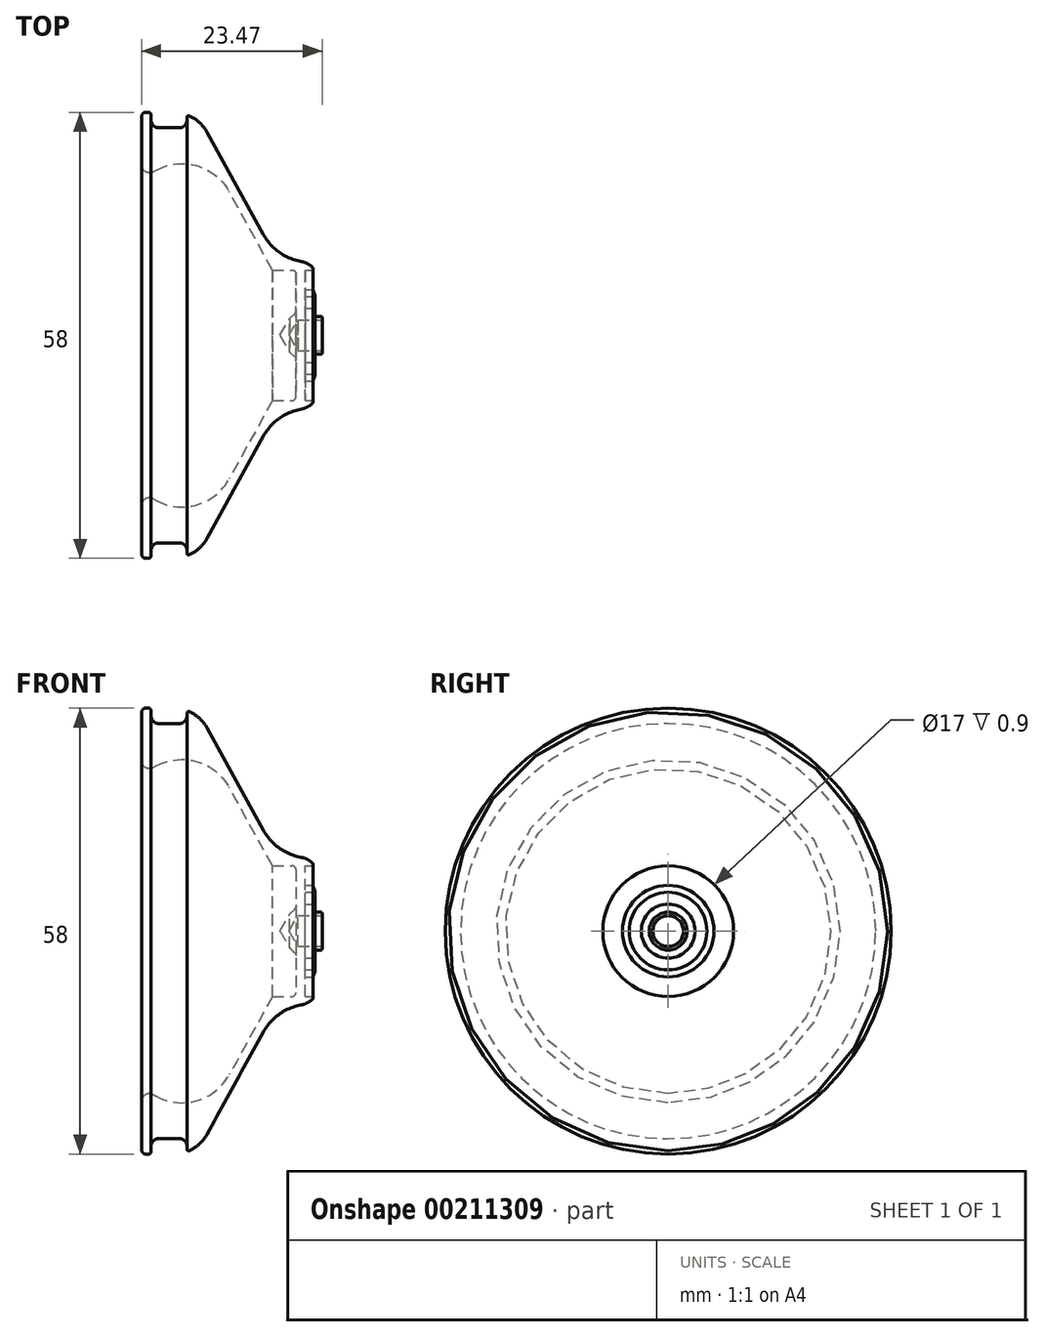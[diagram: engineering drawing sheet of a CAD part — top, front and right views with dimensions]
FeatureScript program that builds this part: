
annotation { "Feature Type Name" : "Feature", "Feature Type Description" : "" }
export const myFeature = defineFeature(function(context is Context, id is Id, definition is map)
    precondition{}
    {
        {
            var Q0;
            Q0=qCreatedBy(makeId("Front.planeOp"),FACE);
            var sketch = newSketch(context, id + "F0", { "sketchPlane" : qUnion([Q0])});
            skLineSegment(sketch, "E0", {"start": v(-1.03, 2) * mm, "end": v(-4.2, 2) * mm});
            skLineSegment(sketch, "E1", {"start": v(-4.2, 2) * mm, "end": v(-5.35, 0) * mm});
            skLineSegment(sketch, "E2", {"start": v(-5.35, 0) * mm, "end": v(-6.5, 0) * mm});
            skLineSegment(sketch, "E3", {"start": v(-6.5, 0) * mm, "end": v(-5.24, 2.2) * mm});
            skLineSegment(sketch, "E4", {"start": v(-4.45, 8.5) * mm, "end": v(-7.5, 8.5) * mm});
            skLineSegment(sketch, "E5", {"start": v(-7.5, 8.5) * mm, "end": v(-13.13, 18.7) * mm});
            skLineSegment(sketch, "E6", {"start": v(-24.5, 22.13) * mm, "end": v(-24.5, 29) * mm});
            skLineSegment(sketch, "E7", {"start": v(-24.5, 29) * mm, "end": v(-23.6, 29) * mm});
            skLineSegment(sketch, "E8", {"start": v(-1.03, 2.47) * mm, "end": v(-2.03, 2.47) * mm});
            skLineSegment(sketch, "E9", {"start": v(-2.03, 2.47) * mm, "end": v(-2.03, 3.5) * mm});
            skLineSegment(sketch, "E10", {"start": v(-2.03, 3.5) * mm, "end": v(-3.25, 3.5) * mm});
            skLineSegment(sketch, "E11", {"start": v(-3.25, 3.5) * mm, "end": v(-3.25, 5.05) * mm});
            skLineSegment(sketch, "E12", {"start": v(-3.25, 5.05) * mm, "end": v(-1.9, 5.05) * mm});
            skLineSegment(sketch, "E13", {"start": v(-2.25, 5.95) * mm, "end": v(-3.25, 5.95) * mm});
            skLineSegment(sketch, "E14", {"start": v(-3.25, 5.95) * mm, "end": v(-3.25, 8.5) * mm});
            skLineSegment(sketch, "E15", {"start": v(-3.25, 8.5) * mm, "end": v(-2.25, 8.5) * mm});
            skLineSegment(sketch, "E16", {"start": v(-2.25, 8.5) * mm, "end": v(-2.25, 9.5) * mm});
            skLineSegment(sketch, "E17", {"start": v(-1.03, 2.47) * mm, "end": v(-1.03, 2) * mm});
            skLineSegment(sketch, "E18", {"start": v(-2.25, 9.5) * mm, "end": v(-2.25, 9.5) * mm});
            skLineSegment(sketch, "E19", {"start": v(-4.45, 8.5) * mm, "end": v(-4.45, 3) * mm});
            skLineSegment(sketch, "E20", {"start": v(-4.45, 3) * mm, "end": v(-5.24, 2.2) * mm});
            skLineSegment(sketch, "E21", {"start": v(-2.25, 9.5) * mm, "end": v(-2.55, 9.5) * mm});
            skLineSegment(sketch, "E22", {"start": v(-16, 26.41) * mm, "end": v(-8.69, 13.12) * mm});
            skPoint(sketch, "E23.visualSharp", {"position": v(-6.7, 9.5) * mm});
            skArc(sketch, "E23.filletArc", {"start": v(-8.69, 13.12) * mm, "mid": v(-6.11, 10.47) * mm, "end": v(-2.55, 9.5) * mm});
            skPoint(sketch, "E24.visualSharp", {"position": v(-17.43, 29) * mm});
            skArc(sketch, "E24.filletArc", {"start": v(-16, 26.41) * mm, "mid": v(-16.99, 27.67) * mm, "end": v(-18.32, 28.55) * mm});
            skLineSegment(sketch, "E25", {"start": v(-23.03, 21.25) * mm, "end": v(-22.57, 21.5) * mm});
            skPoint(sketch, "E26.visualSharp", {"position": v(-16.47, 24.77) * mm});
            skArc(sketch, "E26.filletArc", {"start": v(-13.13, 18.7) * mm, "mid": v(-17.27, 22.04) * mm, "end": v(-22.57, 21.5) * mm});
            skPoint(sketch, "E27.visualSharp", {"position": v(-24.5, 20.46) * mm});
            skLineSegment(sketch, "E28", {"start": v(-23.3, 28.7) * mm, "end": v(-23.3, 28) * mm});
            skLineSegment(sketch, "E29", {"start": v(-22.3, 27) * mm, "end": v(-19.6, 27) * mm});
            skLineSegment(sketch, "E30", {"start": v(-18.6, 28) * mm, "end": v(-18.6, 28.37) * mm});
            skPoint(sketch, "E31.visualSharp", {"position": v(-23.3, 27) * mm});
            skArc(sketch, "E31.filletArc", {"start": v(-23.3, 28) * mm, "mid": v(-23, 27.3) * mm, "end": v(-22.3, 27) * mm});
            skPoint(sketch, "E32.visualSharp", {"position": v(-18.6, 27) * mm});
            skArc(sketch, "E32.filletArc", {"start": v(-19.6, 27) * mm, "mid": v(-18.9, 27.3) * mm, "end": v(-18.6, 28) * mm});
            skPoint(sketch, "E33.visualSharp", {"position": v(-23.3, 29) * mm});
            skArc(sketch, "E33.filletArc", {"start": v(-23.3, 28.7) * mm, "mid": v(-23.39, 28.91) * mm, "end": v(-23.6, 29) * mm});
            skPoint(sketch, "E34.visualSharp", {"position": v(-18.6, 28.67) * mm});
            skArc(sketch, "E34.filletArc", {"start": v(-18.32, 28.55) * mm, "mid": v(-18.5, 28.54) * mm, "end": v(-18.6, 28.37) * mm});
            skArc(sketch, "E35.filletArc", {"start": v(-24.5, 22.13) * mm, "mid": v(-24.01, 21.28) * mm, "end": v(-23.03, 21.25) * mm});
            skLineSegment(sketch, "E36", {"start": v(-2.25, 5.95) * mm, "end": v(-1.9, 5.05) * mm});
            skSolve(sketch);
        }
        {
            var Q0;
            Q0=qSketchRegion(id+"F0",true);
            var Q1;
            Q1=sQuery(id+"F0.wireOp",EDGE,"E2");
            revolve(context, id + "F1", {"entities" : qUnion([Q0]), "axis" : qUnion([Q1]), "revolveType" : RevolveType.FULL});
        }
        {
            var Q0;
            Q0=makeQuery(id+"F1.opRevolve","SWEPT_EDGE",EDGE,{"disambiguationData":[OSD([sQuery(id+"F0.wireOp",EDGE,"E16"),sQuery(id+"F0.wireOp",EDGE,"E21")])]});
            chamfer(context, id + "F2", {"entities" : qUnion([Q0]), "chamferType" : ChamferType.TWO_OFFSETS, "width1" : 0.7 * mm, "oppositeDirection" : false, "width2" : 0.8 * mm, "tangentPropagation" : true});
        }
        {
            var Q0;
            Q0=makeQuery(id+"F2.opChamfer","BLEND_EDGE",EDGE,{"blendedFrom":[makeQuery(id+"F1.opRevolve","SWEPT_EDGE",EDGE,{"disambiguationData":[OSD([sQuery(id+"F0.wireOp",EDGE,"E16"),sQuery(id+"F0.wireOp",EDGE,"E21")])]}),makeQuery(id+"F1.opRevolve","SWEPT_FACE",FACE,{"disambiguationData":[OSD([sQuery(id+"F0.wireOp",EDGE,"E23.filletArc")])]})],"blendedInto":[makeQuery(id+"F1.opRevolve","SWEPT_FACE",FACE,{"disambiguationData":[OSD([sQuery(id+"F0.wireOp",EDGE,"E23.filletArc")])]})]});
            fillet(context, id + "F3", {"entities" : qUnion([Q0]), "radius" : 3 * mm, "tangentPropagation" : true, "allowEdgeOverflow" : false});
        }
        {
            var Q0;
            {var subQ0=sQuery(id+"F0.wireOp",EDGE,"E16");Q0=makeQuery(id+"F2.opChamfer","BLEND_EDGE",EDGE,{"blendedFrom":[makeQuery(id+"F1.opRevolve","SWEPT_EDGE",EDGE,{"disambiguationData":[OSD([subQ0,sQuery(id+"F0.wireOp",EDGE,"E21")])]}),makeQuery(id+"F1.opRevolve","SWEPT_FACE",FACE,{"disambiguationData":[OSD([subQ0])]})],"blendedInto":[makeQuery(id+"F1.opRevolve","SWEPT_FACE",FACE,{"disambiguationData":[OSD([subQ0])]})]});}
            fillet(context, id + "F4", {"entities" : qUnion([Q0]), "radius" : 0.2 * mm, "tangentPropagation" : true, "allowEdgeOverflow" : false});
        }
        {
            var Q0;
            Q0=makeQuery(id+"F1.opRevolve","SWEPT_EDGE",EDGE,{"disambiguationData":[OSD([sQuery(id+"F0.wireOp",EDGE,"E9"),sQuery(id+"F0.wireOp",EDGE,"E10")])]});
            var Q1;
            Q1=makeQuery(id+"F1.opRevolve","SWEPT_EDGE",EDGE,{"disambiguationData":[OSD([sQuery(id+"F0.wireOp",EDGE,"E10"),sQuery(id+"F0.wireOp",EDGE,"E11")])]});
            var Q2;
            Q2=makeQuery(id+"F1.opRevolve","SWEPT_EDGE",EDGE,{"disambiguationData":[OSD([sQuery(id+"F0.wireOp",EDGE,"E12"),sQuery(id+"F0.wireOp",EDGE,"BWx0B6Tx-ZYA4-OBA0-Vl5f-Hy8aU4m60yr2")])]});
            var Q3;
            Q3=makeQuery(id+"F1.opRevolve","SWEPT_EDGE",EDGE,{"disambiguationData":[OSD([sQuery(id+"F0.wireOp",EDGE,"BWx0B6Tx-ZYA4-OBA0-Vl5f-Hy8aU4m60yr2"),sQuery(id+"F0.wireOp",EDGE,"E13")])]});
            var Q4;
            Q4=makeQuery(id+"F1.opRevolve","SWEPT_EDGE",EDGE,{"disambiguationData":[OSD([sQuery(id+"F0.wireOp",EDGE,"E15"),sQuery(id+"F0.wireOp",EDGE,"E16")])]});
            var Q5;
            Q5=makeQuery(id+"F1.opRevolve","SWEPT_EDGE",EDGE,{"disambiguationData":[OSD([sQuery(id+"F0.wireOp",EDGE,"E11"),sQuery(id+"F0.wireOp",EDGE,"E12")])]});
            var Q6;
            Q6=makeQuery(id+"F1.opRevolve","SWEPT_EDGE",EDGE,{"disambiguationData":[OSD([sQuery(id+"F0.wireOp",EDGE,"E8"),sQuery(id+"F0.wireOp",EDGE,"E9")])]});
            fillet(context, id + "F5", {"entities" : qUnion([Q0, Q1, Q2, Q3, Q4, Q5, Q6]), "radius" : 0.1 * mm, "tangentPropagation" : true, "allowEdgeOverflow" : false});
        }
        {
            var Q0;
            Q0=makeQuery(id+"F1.opRevolve","SWEPT_EDGE",EDGE,{"disambiguationData":[OSD([sQuery(id+"F0.wireOp",EDGE,"E8"),sQuery(id+"F0.wireOp",EDGE,"E17")])]});
            fillet(context, id + "F6", {"entities" : qUnion([Q0]), "radius" : 0.2 * mm, "tangentPropagation" : true, "allowEdgeOverflow" : false});
        }
        {
            var Q0;
            Q0=makeQuery(id+"F1.opRevolve","SWEPT_EDGE",EDGE,{"disambiguationData":[OSD([sQuery(id+"F0.wireOp",EDGE,"E6"),sQuery(id+"F0.wireOp",EDGE,"E7")])]});
            fillet(context, id + "F7", {"entities" : qUnion([Q0]), "radius" : 0.5 * mm, "tangentPropagation" : true, "allowEdgeOverflow" : false});
        }
        {
            var Q0;
            Q0=makeQuery(id+"F1.opRevolve","SWEPT_EDGE",EDGE,{"disambiguationData":[OSD([sQuery(id+"F0.wireOp",EDGE,"E19"),sQuery(id+"F0.wireOp",EDGE,"qzoH6j8X-IBxw-pTTz-kvqH-HLydLYGYBeqi")])]});
            fillet(context, id + "F8", {"entities" : qUnion([Q0]), "radius" : 0.5 * mm, "tangentPropagation" : true, "allowEdgeOverflow" : false});
        }
    });
